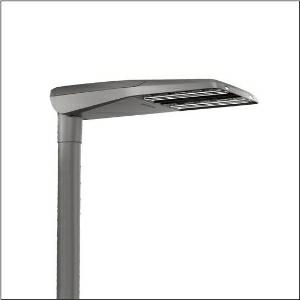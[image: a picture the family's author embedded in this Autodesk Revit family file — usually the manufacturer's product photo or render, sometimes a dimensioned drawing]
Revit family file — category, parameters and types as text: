
# Revit family: streetlight_sl_11_iq_midi___st1_0a_5xc3m51f08le_689c
name_source: partatom
category: Lighting Fixtures
units: mm (PartAtom-declared; Revit-internal decimal feet)

## family parameters
Cut with Voids When Loaded = No
Host = Face
Light Source = No
Part Type = Normal
Room Calculation Point = No
Round Connector Dimension = Use Diameter
Shared = No

## types (1)
- --- (1 x LED, 8920 lm, 60.4 W, 3000K)
    Apparent Load = 60 VA
    CIE Flux Codes = 33 66 96 100 100
    Color Rendering = 70
    Color Temperature = 3000K
    Default Elevation = 1800 mm
    Description = Streetlight SL 11 iQ midi, mast luminaire, primary light control with 3 zone facetted reflector, of plastic, silver coated, highly specular, primary optical cover: cover, of PMMA, transparent, light distribution: ST1.0a, light emission: direct distribution, primary light characteristic: asymmetric, installation type: post-top, side-entry, lamps: LED, High Power LED, rated values: 8.920lm | 60,4W | 147,7lm/W (begin service life); end service life: 8.920lm | 62,5W; at 50% lumin. flux: 4.460lm | 29,6W | 150,7lm/W, colour temperature: 3000K, colour rendering: CRI > 70, light colour: 730, light setting 1 begin service life: 100% | 8.920lm | 60,4W | 147,7lm/W | 3.000K, light setting 1 end service life: 62,5W, further light settings possible, control: optimised constant luminous flux control (CLO 2.0), Street-Remote, Desk-Remote (wireless, voltage-free reading and setting of iQ features in the workshop via application-optimized NFC function/RFID function), Light-Fading, Smart-Wire, Night-Set, Lumen-Switch, Temp-Guard, Auto-Match, with cable H07RN-F 3x 1.5mm², mains connection: 230..240V, AC, 50/60Hz, connection cable pre-assembled, cable length: 8,5m, luminaire housing, of diecast aluminium, powder-coated, SITECO metallic grey (DB 702S), please order mast flange separately, inclination adjustable without tools: 0°, 5°, 10°, 15° (post-top) | 0°, -5°, -10°, -15° (side-entry), sealing non-destructively replaceable, multi-level sealing system, length: 780mm, width: 376mm, height: 118mm, mast flange for spigot size: 42mm (side-entry): 5XC10008XM4, 60/48mm (side-entry/post-top): 5XC10108XM2, 76/60mm (side-entry/post-top): 5XC10108XM1, equipment: standard, protection rating (complete): IP66, insulation class (complete): insulation class II (safety insulation), certification: CE, ENEC, ENEC+, VDE, impact resistance: IK10, permissible operating ambient temperature for outdoor applications: -25..+50°C, standard-compliant lighting for roads and squares, Environmental Product Declaration (EPD) tested and certified by an independent institute, packaging unit: 1 piece

Light Distribution: ST1.0a
    Height = 118 mm
    Lamp = 1 x LED
    Lamp Light Flux = 8920 lm
    Lamp Power = 60.4 W
    Lamp count = 1
    Length = 780 mm
    Luminous efficacy = 148 lm/W
    Manufacturer = Siteco
    ModVariant = No
    Model = 5XC3M51F08LE
    Number of Poles = 1
    OnlyDefault = Yes
    Power Factor = 1
    Product Name = Streetlight SL 11 iQ midi | ST1.0a
    Product group = mast luminaire | pylon top
    ProductGroupID = 6100
    Protection Class = Protection class II
    Protection Degree = IP 66
    RLX_Detail_Level = 1
    RLX_Emergency_Light_Flux = 0 lm
    RLX_Emergency_Type = 0
    RLX_Emergency_Type_DB = No
    RlxData = <blob elided: 70281 chars, md5=807665ca>
    Socket = socket
    Standby Power = 0 W
    System Light Flux = 8920 lm
    System Power = 60 W
    Type Comments = factory setting: luminous flux: 100 % | dim-lin: 254 | 520 mA
    Type Image = l_1005960.jpg
    URL = http://relux.com
    VarID = @adj_092379
    Voltage = 0 V
    Weight = 0.00 kg
    Width = 376 mm

## geometry (parser evidence)
native form markers: Blend x4, Sweep x12
no freeform markers — native parametric forms only
